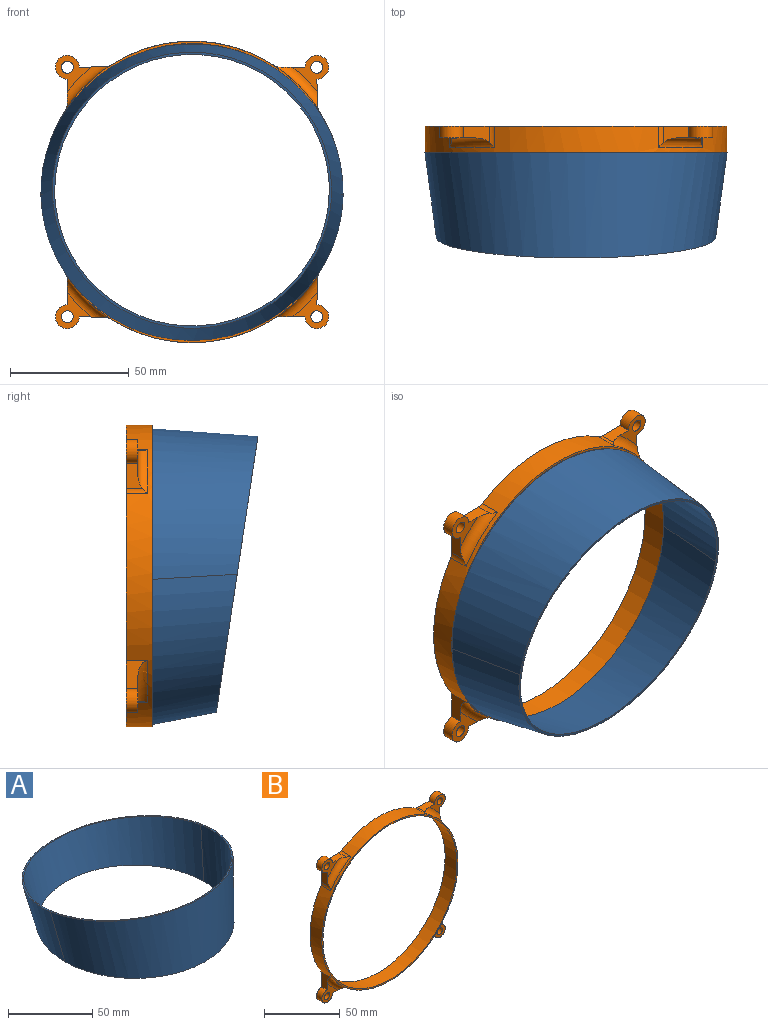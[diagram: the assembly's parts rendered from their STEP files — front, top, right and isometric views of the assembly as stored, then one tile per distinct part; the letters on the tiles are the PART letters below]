
ASSEMBLY  parts=2 mates=1
PART A: 9 faces, bbox 130.1x133.5x160.1 mm
  f0: plane 47.97x4.44mm, normal (0,0.23,0.97), area 44mm2, adj f3,f5,f7
  f1: plane 5.38x0.06mm, normal (0,0,1), area 0.2mm2, adj f2,f4
  f2: plane 7.47x0.72mm, normal (0,1,0), area 4.4mm2, adj f1,f3,f4
  f3: plane 127.26x118.66mm, normal (0,0.15,0.99), area 344.6mm2, adj f0,f2,f4,f5,f6,f7
  f4: bspline ~130x68.36mm, area 7968.8mm2, adj f1,f2,f3,f5,f8
  f5: bspline ~160x130mm, area 5778.2mm2, adj f0,f3,f4,f8
  f6: bspline ~127.78x67.19mm, area 7816.5mm2, adj f3,f7,f8
  f7: bspline ~160x128mm, area 5705.1mm2, adj f0,f3,f6,f8
  f8: plane 117.73x117.71mm, normal (0,0,-1), area 365.9mm2, adj f4,f5,f6,f7
PART B: 35 faces, bbox 127.7x11.8x127.9 mm
  f0: plane 15.23x15.07mm, normal (0,-1,0), area 86.9mm2, adj f11,f12,f13,f17,f34
  f1: plane 15.23x15.07mm, normal (0,-1,0), area 86.9mm2, adj f3,f14,f18,f19,f26
  f2: plane 15.23x15.07mm, normal (0,-1,0), area 86.9mm2, adj f4,f5,f6,f16,f29
  f3: plane 10.57x6.76mm, normal (0,0,1), area 55.8mm2, adj f1,f19,f22,f25,f26
  f4: plane 10.91x6.81mm, normal (-0.01,0,1), area 57.7mm2, adj f2,f5,f22,f27,f29
  f5: cylinder r=5mm len=10mm, axis (0,1,0), area 117.5mm2, adj f2,f4,f6,f22
  f6: plane 10.57x6.76mm, normal (-1,0,0), area 55.8mm2, adj f2,f5,f22,f28,f29
  f7: cylinder r=63.5mm len=127mm, axis (0,1,0), area 3443.5mm2, adj f8,f22,f23,f24,f25,f26,f27,f28
  f8: plane 11.78x9mm, normal (-1,0,0), area 64.8mm2, adj f7,f9,f21,f22,f31
  f9: cylinder r=5mm len=10mm, axis (0,1,0), area 117.5mm2, adj f8,f10,f21,f22
  f10: plane 10.91x6.81mm, normal (-0.01,0,-1), area 57.7mm2, adj f9,f21,f22,f30,f31
  f11: plane 10.57x6.76mm, normal (0,0,-1), area 55.8mm2, adj f0,f12,f22,f32,f34
  f12: cylinder r=5mm len=10mm, axis (0,1,0), area 117.5mm2, adj f0,f11,f13,f22
  f13: plane 10.91x6.81mm, normal (1,0,-0.01), area 57.7mm2, adj f0,f12,f22,f33,f34
  f14: plane 10.91x6.81mm, normal (1,0,0.01), area 57.7mm2, adj f1,f19,f22,f24,f26
  f15: cylinder r=2.5mm len=5mm, axis (0,1,0), area 78.5mm2, adj f21,f22
  f16: cylinder r=2.5mm len=5mm, axis (0,1,0), area 78.5mm2, adj f2,f22
  f17: cylinder r=2.5mm len=5mm, axis (0,1,0), area 78.5mm2, adj f0,f22
  f18: cylinder r=2.5mm len=5mm, axis (0,1,0), area 78.5mm2, adj f1,f22
  f19: cylinder r=5mm len=10mm, axis (0,1,0), area 117.5mm2, adj f1,f3,f14,f22
  f20: cylinder r=62.5mm len=125mm, axis (0,1,0), area 4319.7mm2, adj f22,f23
  f21: plane 15.23x15.07mm, normal (0,-1,0), area 86.9mm2, adj f8,f9,f10,f15,f31
  f22: plane 127x127mm, normal (0,1,0), area 1052.4mm2, adj f3,f4,f5,f6,f7,f8,f9,f10
  f23: plane 127x127mm, normal (0,-1,0), area 395.8mm2, adj f7,f20
  f24: cylinder r=4mm len=9mm, axis (0,1,0), area 17.8mm2, adj f7,f14,f22,f26
  f25: cylinder r=4mm len=9mm, axis (0,1,0), area 18.2mm2, adj f3,f7,f22,f26
  f26: torus R=67.5mm, axis (0,-1,0), area 131.4mm2, adj f1,f3,f7,f14,f24,f25
  f27: cylinder r=4mm len=9mm, axis (0,1,0), area 17.8mm2, adj f4,f7,f22,f29
  f28: cylinder r=4mm len=9mm, axis (0,1,0), area 18.2mm2, adj f6,f7,f22,f29
  f29: torus R=67.5mm, axis (0,-1,0), area 131.4mm2, adj f2,f4,f6,f7,f27,f28
  f30: cylinder r=4mm len=9mm, axis (0,1,0), area 17.8mm2, adj f7,f10,f22,f31
  f31: torus R=67.5mm, axis (0,-1,0), area 130.4mm2, adj f7,f8,f10,f21,f30
  f32: cylinder r=4mm len=9mm, axis (0,1,0), area 18.2mm2, adj f7,f11,f22,f34
  f33: cylinder r=4mm len=9mm, axis (0,1,0), area 17.8mm2, adj f7,f13,f22,f34
  f34: torus R=67.5mm, axis (0,-1,0), area 131.4mm2, adj f0,f7,f11,f13,f32,f33
PLACE A rot(axis=(-1,0,0),81.4deg) t=(35.23,-95.33,176.28)mm
PLACE B t=(76.04,134.64,132.95)mm
MATE planar A.f3 <-> B.f7  axis (0,1,0) through (76.04,123.64,141.26)mm
